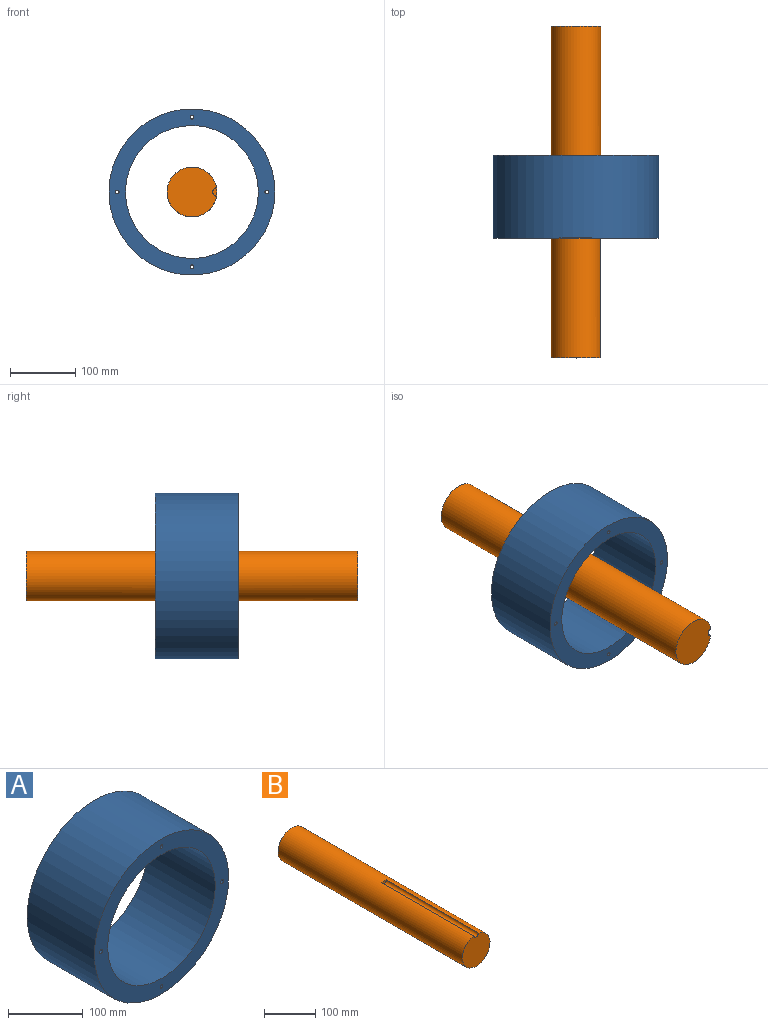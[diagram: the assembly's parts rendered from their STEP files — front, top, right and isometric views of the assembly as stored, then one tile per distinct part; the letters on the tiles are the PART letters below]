
ASSEMBLY  parts=2 mates=1
PART A: 16 faces, bbox 254x127x254 mm
  f0: cylinder r=101.6mm len=203.2mm, axis (0,1,0), area 81073.2mm2, adj f2,f3
  f1: cylinder r=127mm len=254mm, axis (0,1,0), area 101341.5mm2, adj f2,f3
  f2: plane 254x254mm, normal (0,-1,0), area 18146.4mm2, adj f0,f1,f4,f7,f10,f13
  f3: plane 254x254mm, normal (0,1,0), area 17942.8mm2, adj f0,f1,f6,f9,f12,f15
  f4: cylinder r=2.75mm len=122mm, axis (0,1,0), area 2108mm2, adj f2,f5
  f5: plane 9.75x9.75mm, normal (0,1,0), area 50.9mm2, adj f4,f6
  f6: cylinder r=4.88mm len=9.75mm, axis (0,1,0), area 153.2mm2, adj f3,f5
  f7: cylinder r=2.75mm len=122mm, axis (0,1,0), area 2108mm2, adj f2,f8
  f8: plane 9.75x9.75mm, normal (0,1,0), area 50.9mm2, adj f7,f9
  f9: cylinder r=4.88mm len=9.75mm, axis (0,1,0), area 153.2mm2, adj f3,f8
  f10: cylinder r=2.75mm len=122mm, axis (0,1,0), area 2108mm2, adj f2,f11
  f11: plane 9.75x9.75mm, normal (0,1,0), area 50.9mm2, adj f10,f12
  f12: cylinder r=4.88mm len=9.75mm, axis (0,1,0), area 153.2mm2, adj f3,f11
  f13: cylinder r=2.75mm len=122mm, axis (0,1,0), area 2108mm2, adj f2,f14
  f14: plane 9.75x9.75mm, normal (0,1,0), area 50.9mm2, adj f13,f15
  f15: cylinder r=4.88mm len=9.75mm, axis (0,1,0), area 153.2mm2, adj f3,f14
PART B: 5 faces, bbox 76.2x508x76.2 mm
  f0: cylinder r=38.1mm len=508mm, axis (0,1,0), area 118380.2mm2, adj f1,f2,f3,f4
  f1: plane 76.2x75.67mm, normal (0,-1,0), area 4499.3mm2, adj f0,f4
  f2: plane 76.2x76.2mm, normal (0,1,0), area 4560.4mm2, adj f0
  f3: plane 12.66x6.35mm, normal (0,-1,0), area 61.1mm2, adj f0,f4
  f4: cylinder r=6.35mm len=254mm, axis (0,-1,0), area 4797.9mm2, adj f0,f1,f3
PLACE A t=(-59.13,122.11,-51.37)mm fixed
PLACE B rot(axis=(0,1,0),90deg) t=(-59.13,319.73,-51.37)mm
MATE slider A.f0 <-> B.f0  axis (0,1,0) through (-59.13,58.61,-51.37)mm
